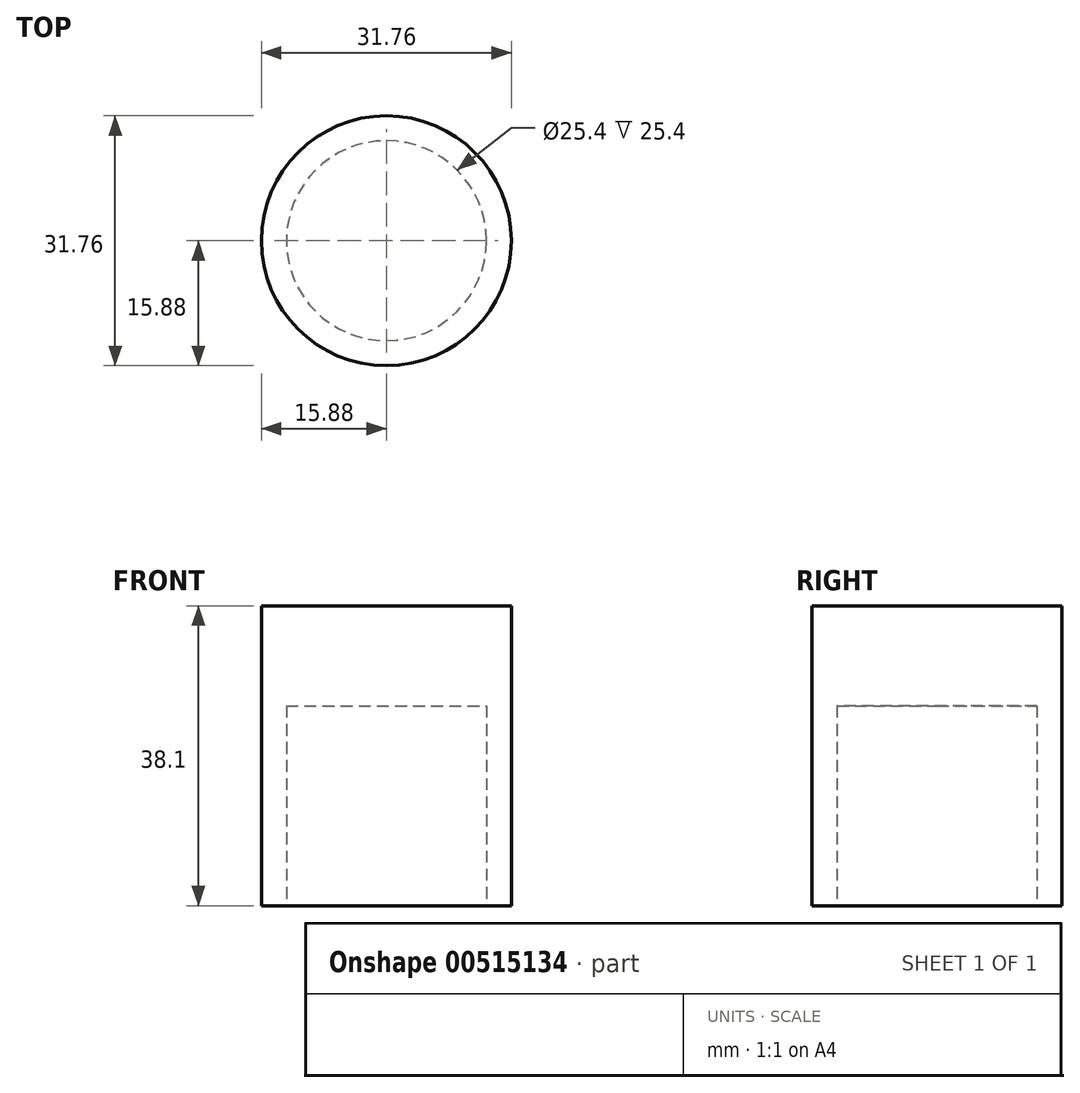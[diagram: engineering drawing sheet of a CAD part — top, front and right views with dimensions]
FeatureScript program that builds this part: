
annotation { "Feature Type Name" : "Feature", "Feature Type Description" : "" }
export const myFeature = defineFeature(function(context is Context, id is Id, definition is map)
    precondition{}
    {
        {
            var Q0;
            Q0=qCreatedBy(makeId("Top.planeOp"),FACE);
            var sketch = newSketch(context, id + "F0", { "sketchPlane" : qUnion([Q0])});
            skCircle(sketch, "E0", {"center": v(0, 0) * mm, "radius": 15.88 * mm});
            skSolve(sketch);
        }
        {
            var Q0;
            Q0 = qSketchRegion(id + "F0", true);
            extrude(context, id + "F1", {"entities" : qUnion([Q0]), "depth" : 38.1 * mm, "offsetDistance" : 25.4 * mm});
        }
        {
            var Q0;
            Q0=makeQuery(id+"F1.opExtrude","CAP_FACE",FACE,{"disambiguationData":[OSD([sQuery(id+"F0.wireOp",EDGE,"E0")])],"isStart":true});
            var sketch = newSketch(context, id + "F2", { "sketchPlane" : qUnion([Q0])});
            skCircle(sketch, "E1", {"center": v(0, 0) * mm, "radius": 12.7 * mm});
            skSolve(sketch);
        }
        {
            var Q0;
            Q0 = qSketchRegion(id + "F2", true);
            extrude(context, id + "F3", {"entities" : qUnion([Q0]), "operationType" : NewBodyOperationType.REMOVE, "oppositeDirection" : true, "depth" : 25.4 * mm, "offsetDistance" : 25.4 * mm});
        }
    });
